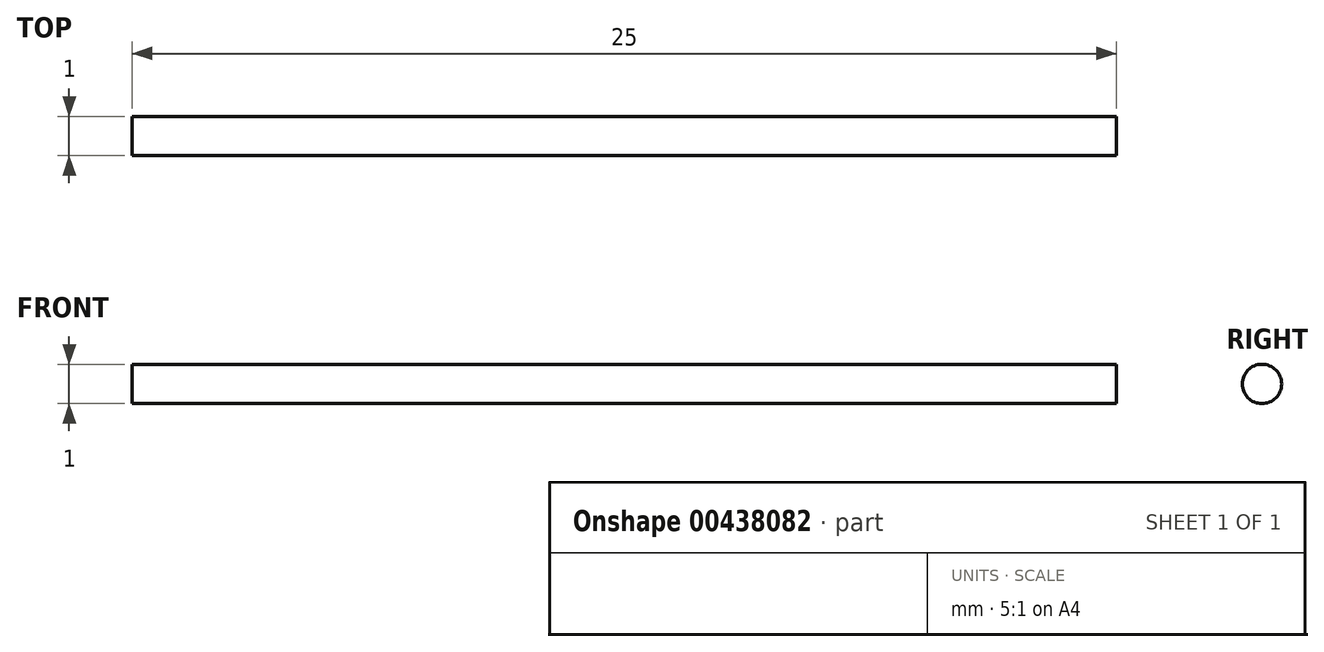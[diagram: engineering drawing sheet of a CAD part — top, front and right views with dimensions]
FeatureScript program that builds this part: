
annotation { "Feature Type Name" : "Feature", "Feature Type Description" : "" }
export const myFeature = defineFeature(function(context is Context, id is Id, definition is map)
    precondition{}
    {
        {
            var Q0;
            Q0=qCreatedBy(makeId("Right.planeOp"),FACE);
            var sketch = newSketch(context, id + "F0", { "sketchPlane" : qUnion([Q0])});
            skCircle(sketch, "E0", {"center": v(0, 0) * mm, "radius": 0.5 * mm});
            skSolve(sketch);
        }
        {
            var Q0;
            Q0=qSketchRegion(id+"F0",true);
            extrude(context, id + "F1", {"entities" : qUnion([Q0]), "depth" : 25 * mm});
        }
    });
